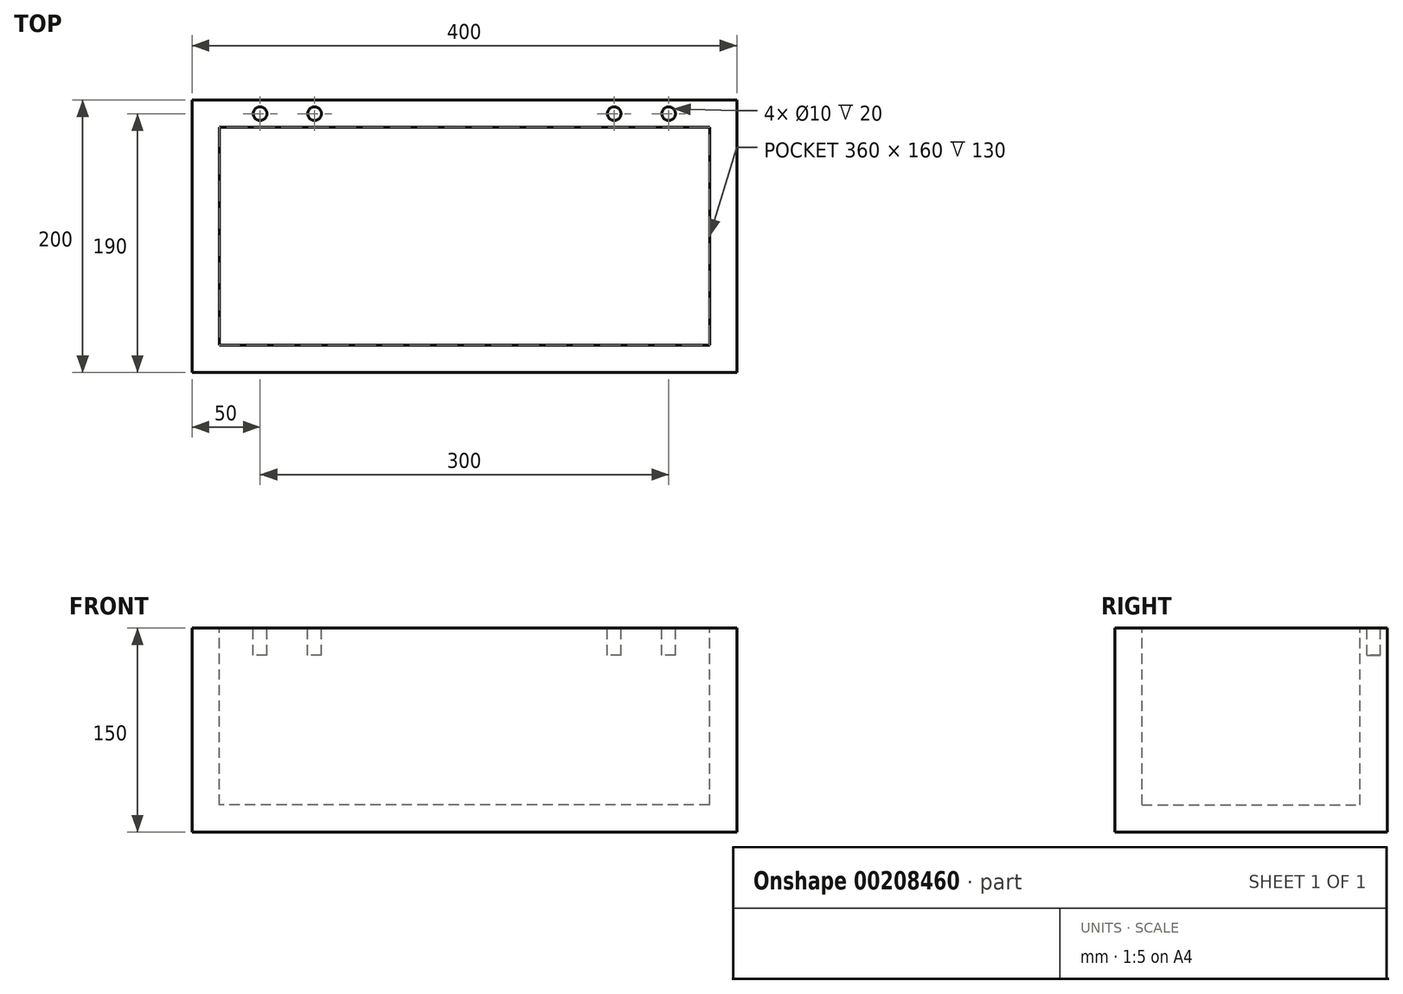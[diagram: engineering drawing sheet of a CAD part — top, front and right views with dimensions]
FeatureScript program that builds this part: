
annotation { "Feature Type Name" : "Feature", "Feature Type Description" : "" }
export const myFeature = defineFeature(function(context is Context, id is Id, definition is map)
    precondition{}
    {
        {
            var Q0;
            Q0=qCreatedBy(makeId("Top.planeOp"),FACE);
            var sketch = newSketch(context, id + "F0", { "sketchPlane" : qUnion([Q0])});
            skLineSegment(sketch, "E0.bottom", {"start": v(200, -100) * mm, "end": v(-200, -100) * mm});
            skLineSegment(sketch, "E0.top", {"start": v(200, 100) * mm, "end": v(-200, 100) * mm});
            skLineSegment(sketch, "E0.left", {"start": v(200, -100) * mm, "end": v(200, 100) * mm});
            skLineSegment(sketch, "E0.right", {"start": v(-200, -100) * mm, "end": v(-200, 100) * mm});
            skPoint(sketch, "E0.middle", {"position": v(0, 0) * mm});
            skSolve(sketch);
        }
        {
            var Q0;
            Q0=qSketchRegion(id+"F0",true);
            extrude(context, id + "F1", {"entities" : qUnion([Q0]), "depth" : 150 * mm});
        }
        {
            var Q0;
            Q0=makeQuery(id+"F1.opExtrude","CAP_FACE",FACE,{"disambiguationData":[OSD([sQuery(id+"F0.wireOp",EDGE,"E0.bottom"),sQuery(id+"F0.wireOp",EDGE,"E0.top"),sQuery(id+"F0.wireOp",EDGE,"E0.left"),sQuery(id+"F0.wireOp",EDGE,"E0.right")])],"isStart":false});
            var sketch = newSketch(context, id + "F2", { "sketchPlane" : qUnion([Q0])});
            skLineSegment(sketch, "E1.bottom", {"start": v(180, -80) * mm, "end": v(-180, -80) * mm});
            skLineSegment(sketch, "E1.top", {"start": v(180, 80) * mm, "end": v(-180, 80) * mm});
            skLineSegment(sketch, "E1.left", {"start": v(180, -80) * mm, "end": v(180, 80) * mm});
            skLineSegment(sketch, "E1.right", {"start": v(-180, -80) * mm, "end": v(-180, 80) * mm});
            skPoint(sketch, "E1.middle", {"position": v(0, 0) * mm});
            skSolve(sketch);
        }
        {
            var Q0;
            Q0=makeQuery(id+"F2.imprint","IMPRINT",FACE,{"disambiguationData":[TD([[makeQuery(id+"F2.imprint","IMPRINT",EDGE,{"derivedFrom":sQuery(id+"F2.wireOp",EDGE,"E1.bottom")}),-1.0]])]});
            extrude(context, id + "F3", {"entities" : qUnion([Q0]), "operationType" : NewBodyOperationType.REMOVE, "oppositeDirection" : true, "depth" : 130 * mm});
        }
        {
            var Q0;
            Q0=makeQuery(id+"F1.opExtrude","CAP_FACE",FACE,{"disambiguationData":[OSD([sQuery(id+"F0.wireOp",EDGE,"E0.bottom"),sQuery(id+"F0.wireOp",EDGE,"E0.top"),sQuery(id+"F0.wireOp",EDGE,"E0.left"),sQuery(id+"F0.wireOp",EDGE,"E0.right")])],"isStart":false});
            var sketch = newSketch(context, id + "F4", { "sketchPlane" : qUnion([Q0])});
            skCircle(sketch, "E2", {"center": v(-150, 90) * mm, "radius": 5 * mm});
            skCircle(sketch, "E3", {"center": v(-110, 90) * mm, "radius": 5 * mm});
            skLineSegment(sketch, "E4", {"start": v(0, 80) * mm, "end": v(0, 100) * mm, "construction": true});
            skCircle(sketch, "E5.MirrorC", {"center": v(110, 90) * mm, "radius": 5 * mm});
            skCircle(sketch, "E6.MirrorC", {"center": v(150, 90) * mm, "radius": 5 * mm});
            skSolve(sketch);
        }
        {
            var Q0;
            Q0=qSketchRegion(id+"F4",true);
            extrude(context, id + "F5", {"entities" : qUnion([Q0]), "operationType" : NewBodyOperationType.REMOVE, "oppositeDirection" : true, "depth" : 20 * mm});
        }
    });
